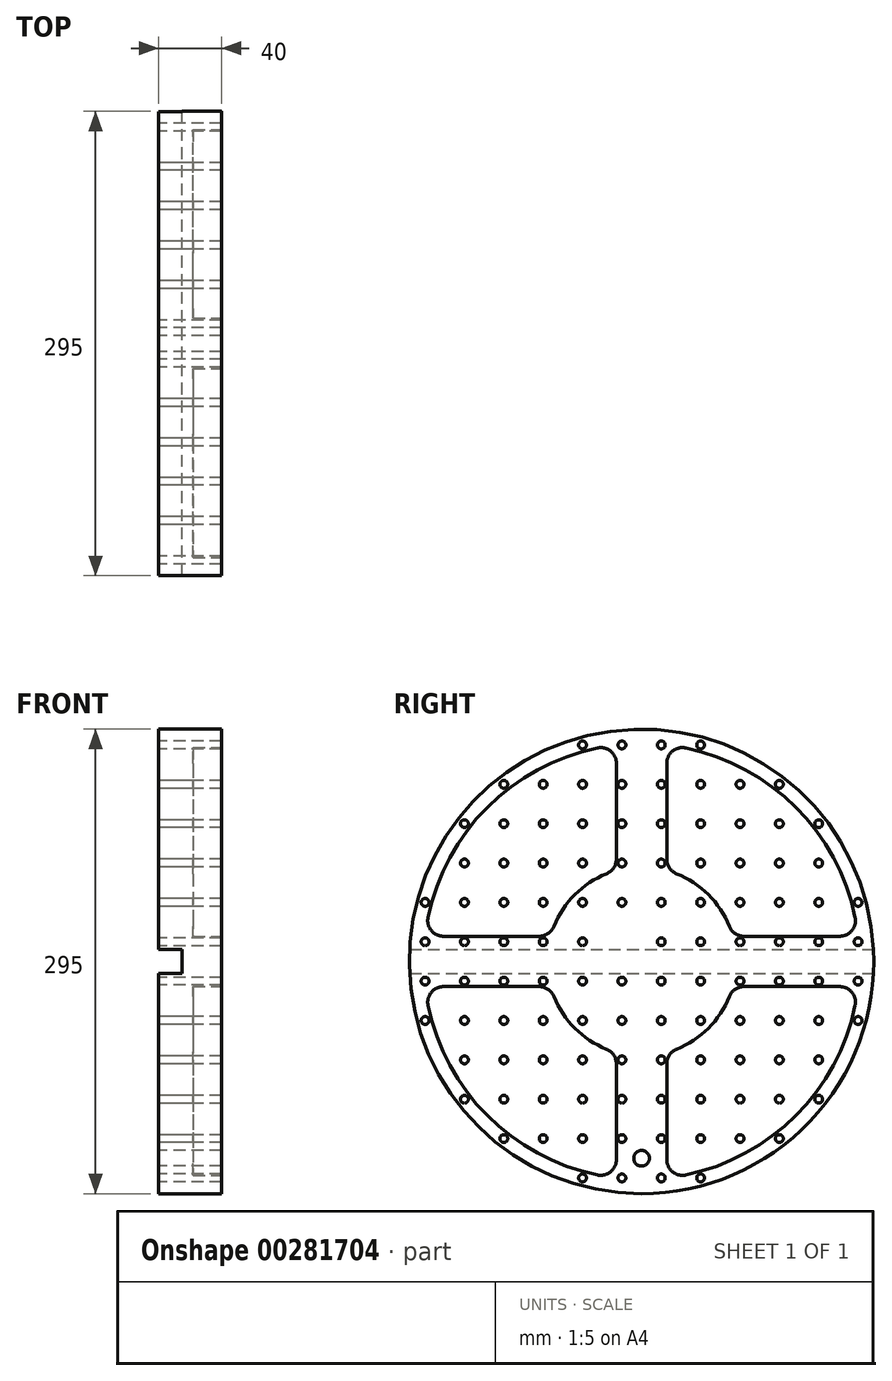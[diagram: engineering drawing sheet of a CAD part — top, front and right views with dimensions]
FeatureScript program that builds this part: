
annotation { "Feature Type Name" : "Feature", "Feature Type Description" : "" }
export const myFeature = defineFeature(function(context is Context, id is Id, definition is map)
    precondition{}
    {
        {
            var Q0;
            Q0=qCreatedBy(makeId("Right.planeOp"),FACE);
            var sketch = newSketch(context, id + "F0", { "sketchPlane" : qUnion([Q0])});
            skCircle(sketch, "E0", {"center": v(0, 0) * mm, "radius": 147.5 * mm});
            skLineSegment(sketch, "E1", {"start": v(-147.5, 0) * mm, "end": v(106.1, 0) * mm, "construction": true});
            skLineSegment(sketch, "E2", {"start": v(106.1, 0) * mm, "end": v(147.5, 0) * mm, "construction": true});
            skLineSegment(sketch, "E3", {"start": v(-147.3, 7.5) * mm, "end": v(147.3, 7.5) * mm});
            skLineSegment(sketch, "E4", {"start": v(-147.3, -7.5) * mm, "end": v(147.3, -7.5) * mm});
            skPoint(sketch, "E5.orphan", {"position": v(-155.54, -7.5) * mm});
            skCircle(sketch, "E6", {"center": v(-12.5, -12.5) * mm, "radius": 2.5 * mm});
            skCircle(sketch, "E7.0.1.0", {"center": v(-12.5, -37.5) * mm, "radius": 2.5 * mm});
            skCircle(sketch, "E7.0.2.0", {"center": v(-12.5, -62.5) * mm, "radius": 2.5 * mm});
            skCircle(sketch, "E7.0.3.0", {"center": v(-12.5, -87.5) * mm, "radius": 2.5 * mm});
            skCircle(sketch, "E7.1.0.0", {"center": v(-37.5, -12.5) * mm, "radius": 2.5 * mm});
            skCircle(sketch, "E7.1.1.0", {"center": v(-37.5, -37.5) * mm, "radius": 2.5 * mm});
            skCircle(sketch, "E7.1.2.0", {"center": v(-37.5, -62.5) * mm, "radius": 2.5 * mm});
            skCircle(sketch, "E7.1.3.0", {"center": v(-37.5, -87.5) * mm, "radius": 2.5 * mm});
            skCircle(sketch, "E7.2.0.0", {"center": v(-62.5, -12.5) * mm, "radius": 2.5 * mm});
            skCircle(sketch, "E7.2.1.0", {"center": v(-62.5, -37.5) * mm, "radius": 2.5 * mm});
            skCircle(sketch, "E7.2.2.0", {"center": v(-62.5, -62.5) * mm, "radius": 2.5 * mm});
            skCircle(sketch, "E7.2.3.0", {"center": v(-62.5, -87.5) * mm, "radius": 2.5 * mm});
            skCircle(sketch, "E7.3.0.0", {"center": v(-87.5, -12.5) * mm, "radius": 2.5 * mm});
            skCircle(sketch, "E7.3.1.0", {"center": v(-87.5, -37.5) * mm, "radius": 2.5 * mm});
            skCircle(sketch, "E7.3.2.0", {"center": v(-87.5, -62.5) * mm, "radius": 2.5 * mm});
            skCircle(sketch, "E7.3.3.0", {"center": v(-87.5, -87.5) * mm, "radius": 2.5 * mm});
            skLineSegment(sketch, "E7.direction1", {"start": v(-12.5, -12.5) * mm, "end": v(-37.5, -12.5) * mm, "construction": true});
            skLineSegment(sketch, "E7.direction2", {"start": v(-12.5, -12.5) * mm, "end": v(-12.5, -37.5) * mm, "construction": true});
            skCircle(sketch, "E8.0.0.4", {"center": v(-12.5, -112.5) * mm, "radius": 2.5 * mm});
            skCircle(sketch, "E8.0.1.4", {"center": v(-37.5, -112.5) * mm, "radius": 2.5 * mm});
            skCircle(sketch, "E8.0.2.4", {"center": v(-62.5, -112.5) * mm, "radius": 2.5 * mm});
            skCircle(sketch, "E8.0.3.4", {"center": v(-87.5, -112.5) * mm, "radius": 2.5 * mm});
            skCircle(sketch, "E9.0.0.5", {"center": v(-12.5, -137.5) * mm, "radius": 2.5 * mm});
            skCircle(sketch, "E9.0.1.5", {"center": v(-37.5, -137.5) * mm, "radius": 2.5 * mm});
            skCircle(sketch, "E9.0.2.5", {"center": v(-62.5, -137.5) * mm, "radius": 2.5 * mm});
            skCircle(sketch, "E9.0.3.5", {"center": v(-87.5, -137.5) * mm, "radius": 2.5 * mm});
            skCircle(sketch, "E10.0.4.0", {"center": v(-112.5, -12.5) * mm, "radius": 2.5 * mm});
            skCircle(sketch, "E10.0.4.1", {"center": v(-112.5, -37.5) * mm, "radius": 2.5 * mm});
            skCircle(sketch, "E10.0.4.2", {"center": v(-112.5, -62.5) * mm, "radius": 2.5 * mm});
            skCircle(sketch, "E10.0.4.3", {"center": v(-112.5, -87.5) * mm, "radius": 2.5 * mm});
            skCircle(sketch, "E10.0.4.4", {"center": v(-112.5, -112.5) * mm, "radius": 2.5 * mm});
            skCircle(sketch, "E10.0.4.5", {"center": v(-112.5, -137.5) * mm, "radius": 2.5 * mm});
            skCircle(sketch, "E10.0.5.0", {"center": v(-137.5, -12.5) * mm, "radius": 2.5 * mm});
            skCircle(sketch, "E10.0.5.1", {"center": v(-137.5, -37.5) * mm, "radius": 2.5 * mm});
            skCircle(sketch, "E10.0.5.2", {"center": v(-137.5, -62.5) * mm, "radius": 2.5 * mm});
            skCircle(sketch, "E10.0.5.3", {"center": v(-137.5, -87.5) * mm, "radius": 2.5 * mm});
            skCircle(sketch, "E10.0.5.4", {"center": v(-137.5, -112.5) * mm, "radius": 2.5 * mm});
            skCircle(sketch, "E10.0.5.5", {"center": v(-137.5, -137.5) * mm, "radius": 2.5 * mm});
            skCircle(sketch, "E11.MirrorC", {"center": v(87.5, -112.5) * mm, "radius": 2.5 * mm});
            skCircle(sketch, "E12.MirrorC", {"center": v(12.5, -112.5) * mm, "radius": 2.5 * mm});
            skCircle(sketch, "E13.MirrorC", {"center": v(62.5, -112.5) * mm, "radius": 2.5 * mm});
            skCircle(sketch, "E14.MirrorC", {"center": v(12.5, -12.5) * mm, "radius": 2.5 * mm});
            skCircle(sketch, "E15.MirrorC", {"center": v(37.5, -112.5) * mm, "radius": 2.5 * mm});
            skCircle(sketch, "E16.MirrorC", {"center": v(37.5, -12.5) * mm, "radius": 2.5 * mm});
            skCircle(sketch, "E17.MirrorC", {"center": v(12.5, -37.5) * mm, "radius": 2.5 * mm});
            skCircle(sketch, "E18.MirrorC", {"center": v(37.5, -87.5) * mm, "radius": 2.5 * mm});
            skCircle(sketch, "E19.MirrorC", {"center": v(12.5, -87.5) * mm, "radius": 2.5 * mm});
            skCircle(sketch, "E20.MirrorC", {"center": v(37.5, -137.5) * mm, "radius": 2.5 * mm});
            skCircle(sketch, "E21.MirrorC", {"center": v(62.5, -87.5) * mm, "radius": 2.5 * mm});
            skCircle(sketch, "E22.MirrorC", {"center": v(12.5, -62.5) * mm, "radius": 2.5 * mm});
            skCircle(sketch, "E23.MirrorC", {"center": v(87.5, -37.5) * mm, "radius": 2.5 * mm});
            skCircle(sketch, "E24.MirrorC", {"center": v(112.5, -37.5) * mm, "radius": 2.5 * mm});
            skCircle(sketch, "E25.MirrorC", {"center": v(112.5, -112.5) * mm, "radius": 2.5 * mm});
            skCircle(sketch, "E26.MirrorC", {"center": v(137.5, -62.5) * mm, "radius": 2.5 * mm});
            skCircle(sketch, "E27.MirrorC", {"center": v(87.5, -87.5) * mm, "radius": 2.5 * mm});
            skCircle(sketch, "E28.MirrorC", {"center": v(87.5, -12.5) * mm, "radius": 2.5 * mm});
            skCircle(sketch, "E29.MirrorC", {"center": v(137.5, -12.5) * mm, "radius": 2.5 * mm});
            skCircle(sketch, "E30.MirrorC", {"center": v(137.5, -137.5) * mm, "radius": 2.5 * mm});
            skCircle(sketch, "E31.MirrorC", {"center": v(112.5, -137.5) * mm, "radius": 2.5 * mm});
            skCircle(sketch, "E32.MirrorC", {"center": v(87.5, -137.5) * mm, "radius": 2.5 * mm});
            skCircle(sketch, "E33.MirrorC", {"center": v(137.5, -87.5) * mm, "radius": 2.5 * mm});
            skCircle(sketch, "E34.MirrorC", {"center": v(62.5, -62.5) * mm, "radius": 2.5 * mm});
            skCircle(sketch, "E35.MirrorC", {"center": v(12.5, -137.5) * mm, "radius": 2.5 * mm});
            skCircle(sketch, "E36.MirrorC", {"center": v(137.5, -112.5) * mm, "radius": 2.5 * mm});
            skCircle(sketch, "E37.MirrorC", {"center": v(112.5, -87.5) * mm, "radius": 2.5 * mm});
            skCircle(sketch, "E38.MirrorC", {"center": v(112.5, -62.5) * mm, "radius": 2.5 * mm});
            skCircle(sketch, "E39.MirrorC", {"center": v(37.5, -62.5) * mm, "radius": 2.5 * mm});
            skCircle(sketch, "E40.MirrorC", {"center": v(62.5, -137.5) * mm, "radius": 2.5 * mm});
            skCircle(sketch, "E41.MirrorC", {"center": v(62.5, -37.5) * mm, "radius": 2.5 * mm});
            skCircle(sketch, "E42.MirrorC", {"center": v(137.5, -37.5) * mm, "radius": 2.5 * mm});
            skCircle(sketch, "E43.MirrorC", {"center": v(112.5, -12.5) * mm, "radius": 2.5 * mm});
            skCircle(sketch, "E44.MirrorC", {"center": v(87.5, -62.5) * mm, "radius": 2.5 * mm});
            skCircle(sketch, "E45.MirrorC", {"center": v(62.5, -12.5) * mm, "radius": 2.5 * mm});
            skCircle(sketch, "E46.MirrorC", {"center": v(37.5, -37.5) * mm, "radius": 2.5 * mm});
            skLineSegment(sketch, "E47.MirrorCS", {"start": v(12.5, -12.5) * mm, "end": v(12.5, -37.5) * mm, "construction": true});
            skLineSegment(sketch, "E48.MirrorCS", {"start": v(12.5, -12.5) * mm, "end": v(37.5, -12.5) * mm, "construction": true});
            skLineSegment(sketch, "E49.MirrorCS", {"start": v(147.5, 0) * mm, "end": v(-106.1, 0) * mm, "construction": true});
            skCircle(sketch, "E50.MirrorC", {"center": v(-87.5, 112.5) * mm, "radius": 2.5 * mm});
            skCircle(sketch, "E51.MirrorC", {"center": v(-12.5, 12.5) * mm, "radius": 2.5 * mm});
            skCircle(sketch, "E52.MirrorC", {"center": v(87.5, 112.5) * mm, "radius": 2.5 * mm});
            skCircle(sketch, "E53.MirrorC", {"center": v(62.5, 112.5) * mm, "radius": 2.5 * mm});
            skCircle(sketch, "E54.MirrorC", {"center": v(12.5, 112.5) * mm, "radius": 2.5 * mm});
            skCircle(sketch, "E55.MirrorC", {"center": v(12.5, 12.5) * mm, "radius": 2.5 * mm});
            skCircle(sketch, "E56.MirrorC", {"center": v(-62.5, 112.5) * mm, "radius": 2.5 * mm});
            skCircle(sketch, "E57.MirrorC", {"center": v(37.5, 112.5) * mm, "radius": 2.5 * mm});
            skCircle(sketch, "E58.MirrorC", {"center": v(-37.5, 112.5) * mm, "radius": 2.5 * mm});
            skCircle(sketch, "E59.MirrorC", {"center": v(-12.5, 112.5) * mm, "radius": 2.5 * mm});
            skCircle(sketch, "E60.MirrorC", {"center": v(-12.5, 37.5) * mm, "radius": 2.5 * mm});
            skCircle(sketch, "E61.MirrorC", {"center": v(-37.5, 12.5) * mm, "radius": 2.5 * mm});
            skCircle(sketch, "E62.MirrorC", {"center": v(37.5, 12.5) * mm, "radius": 2.5 * mm});
            skCircle(sketch, "E63.MirrorC", {"center": v(12.5, 37.5) * mm, "radius": 2.5 * mm});
            skCircle(sketch, "E64.MirrorC", {"center": v(-62.5, 137.5) * mm, "radius": 2.5 * mm});
            skCircle(sketch, "E65.MirrorC", {"center": v(37.5, 87.5) * mm, "radius": 2.5 * mm});
            skCircle(sketch, "E66.MirrorC", {"center": v(-62.5, 37.5) * mm, "radius": 2.5 * mm});
            skCircle(sketch, "E67.MirrorC", {"center": v(37.5, 137.5) * mm, "radius": 2.5 * mm});
            skCircle(sketch, "E68.MirrorC", {"center": v(112.5, 12.5) * mm, "radius": 2.5 * mm});
            skCircle(sketch, "E69.MirrorC", {"center": v(62.5, 37.5) * mm, "radius": 2.5 * mm});
            skCircle(sketch, "E70.MirrorC", {"center": v(137.5, 37.5) * mm, "radius": 2.5 * mm});
            skCircle(sketch, "E71.MirrorC", {"center": v(37.5, 37.5) * mm, "radius": 2.5 * mm});
            skCircle(sketch, "E72.MirrorC", {"center": v(12.5, 137.5) * mm, "radius": 2.5 * mm});
            skCircle(sketch, "E73.MirrorC", {"center": v(137.5, 137.5) * mm, "radius": 2.5 * mm});
            skCircle(sketch, "E74.MirrorC", {"center": v(62.5, 87.5) * mm, "radius": 2.5 * mm});
            skCircle(sketch, "E75.MirrorC", {"center": v(-62.5, 87.5) * mm, "radius": 2.5 * mm});
            skCircle(sketch, "E76.MirrorC", {"center": v(-87.5, 87.5) * mm, "radius": 2.5 * mm});
            skCircle(sketch, "E77.MirrorC", {"center": v(37.5, 62.5) * mm, "radius": 2.5 * mm});
            skCircle(sketch, "E78.MirrorC", {"center": v(112.5, 37.5) * mm, "radius": 2.5 * mm});
            skCircle(sketch, "E79.MirrorC", {"center": v(-112.5, 87.5) * mm, "radius": 2.5 * mm});
            skCircle(sketch, "E80.MirrorC", {"center": v(112.5, 112.5) * mm, "radius": 2.5 * mm});
            skCircle(sketch, "E81.MirrorC", {"center": v(-112.5, 12.5) * mm, "radius": 2.5 * mm});
            skCircle(sketch, "E82.MirrorC", {"center": v(-112.5, 37.5) * mm, "radius": 2.5 * mm});
            skCircle(sketch, "E83.MirrorC", {"center": v(-37.5, 37.5) * mm, "radius": 2.5 * mm});
            skCircle(sketch, "E84.MirrorC", {"center": v(62.5, 137.5) * mm, "radius": 2.5 * mm});
            skCircle(sketch, "E85.MirrorC", {"center": v(-87.5, 137.5) * mm, "radius": 2.5 * mm});
            skCircle(sketch, "E86.MirrorC", {"center": v(112.5, 62.5) * mm, "radius": 2.5 * mm});
            skCircle(sketch, "E87.MirrorC", {"center": v(-37.5, 137.5) * mm, "radius": 2.5 * mm});
            skCircle(sketch, "E88.MirrorC", {"center": v(87.5, 62.5) * mm, "radius": 2.5 * mm});
            skCircle(sketch, "E89.MirrorC", {"center": v(-62.5, 12.5) * mm, "radius": 2.5 * mm});
            skCircle(sketch, "E90.MirrorC", {"center": v(137.5, 87.5) * mm, "radius": 2.5 * mm});
            skCircle(sketch, "E91.MirrorC", {"center": v(-12.5, 137.5) * mm, "radius": 2.5 * mm});
            skCircle(sketch, "E92.MirrorC", {"center": v(-137.5, 87.5) * mm, "radius": 2.5 * mm});
            skCircle(sketch, "E93.MirrorC", {"center": v(137.5, 12.5) * mm, "radius": 2.5 * mm});
            skCircle(sketch, "E94.MirrorC", {"center": v(-137.5, 12.5) * mm, "radius": 2.5 * mm});
            skCircle(sketch, "E95.MirrorC", {"center": v(87.5, 87.5) * mm, "radius": 2.5 * mm});
            skCircle(sketch, "E96.MirrorC", {"center": v(12.5, 62.5) * mm, "radius": 2.5 * mm});
            skCircle(sketch, "E97.MirrorC", {"center": v(-12.5, 62.5) * mm, "radius": 2.5 * mm});
            skCircle(sketch, "E98.MirrorC", {"center": v(-137.5, 62.5) * mm, "radius": 2.5 * mm});
            skCircle(sketch, "E99.MirrorC", {"center": v(62.5, 12.5) * mm, "radius": 2.5 * mm});
            skCircle(sketch, "E100.MirrorC", {"center": v(-62.5, 62.5) * mm, "radius": 2.5 * mm});
            skCircle(sketch, "E101.MirrorC", {"center": v(87.5, 12.5) * mm, "radius": 2.5 * mm});
            skCircle(sketch, "E102.MirrorC", {"center": v(-37.5, 87.5) * mm, "radius": 2.5 * mm});
            skCircle(sketch, "E103.MirrorC", {"center": v(-87.5, 37.5) * mm, "radius": 2.5 * mm});
            skCircle(sketch, "E104.MirrorC", {"center": v(12.5, 87.5) * mm, "radius": 2.5 * mm});
            skCircle(sketch, "E105.MirrorC", {"center": v(112.5, 87.5) * mm, "radius": 2.5 * mm});
            skCircle(sketch, "E106.MirrorC", {"center": v(-112.5, 62.5) * mm, "radius": 2.5 * mm});
            skCircle(sketch, "E107.MirrorC", {"center": v(-87.5, 62.5) * mm, "radius": 2.5 * mm});
            skCircle(sketch, "E108.MirrorC", {"center": v(-137.5, 137.5) * mm, "radius": 2.5 * mm});
            skCircle(sketch, "E109.MirrorC", {"center": v(-112.5, 112.5) * mm, "radius": 2.5 * mm});
            skCircle(sketch, "E110.MirrorC", {"center": v(-112.5, 137.5) * mm, "radius": 2.5 * mm});
            skCircle(sketch, "E111.MirrorC", {"center": v(137.5, 62.5) * mm, "radius": 2.5 * mm});
            skCircle(sketch, "E112.MirrorC", {"center": v(-12.5, 87.5) * mm, "radius": 2.5 * mm});
            skCircle(sketch, "E113.MirrorC", {"center": v(-87.5, 12.5) * mm, "radius": 2.5 * mm});
            skCircle(sketch, "E114.MirrorC", {"center": v(-137.5, 112.5) * mm, "radius": 2.5 * mm});
            skCircle(sketch, "E115.MirrorC", {"center": v(137.5, 112.5) * mm, "radius": 2.5 * mm});
            skCircle(sketch, "E116.MirrorC", {"center": v(62.5, 62.5) * mm, "radius": 2.5 * mm});
            skCircle(sketch, "E117.MirrorC", {"center": v(87.5, 37.5) * mm, "radius": 2.5 * mm});
            skCircle(sketch, "E118.MirrorC", {"center": v(-137.5, 37.5) * mm, "radius": 2.5 * mm});
            skCircle(sketch, "E119.MirrorC", {"center": v(-37.5, 62.5) * mm, "radius": 2.5 * mm});
            skCircle(sketch, "E120.MirrorC", {"center": v(112.5, 137.5) * mm, "radius": 2.5 * mm});
            skCircle(sketch, "E121.MirrorC", {"center": v(87.5, 137.5) * mm, "radius": 2.5 * mm});
            skLineSegment(sketch, "E122.MirrorCS", {"start": v(12.5, 12.5) * mm, "end": v(12.5, 37.5) * mm, "construction": true});
            skLineSegment(sketch, "E123.MirrorCS", {"start": v(12.5, 12.5) * mm, "end": v(37.5, 12.5) * mm, "construction": true});
            skLineSegment(sketch, "E124.MirrorCS", {"start": v(-12.5, 12.5) * mm, "end": v(-37.5, 12.5) * mm, "construction": true});
            skLineSegment(sketch, "E125.MirrorCS", {"start": v(-12.5, 12.5) * mm, "end": v(-12.5, 37.5) * mm, "construction": true});
            skPoint(sketch, "E126.MirrorP", {"position": v(-155.54, 7.5) * mm});
            skLineSegment(sketch, "E127", {"start": v(12.5, -112.5) * mm, "end": v(-12.5, -137.5) * mm, "construction": true});
            skLineSegment(sketch, "E128", {"start": v(-12.5, -112.5) * mm, "end": v(12.5, -137.5) * mm, "construction": true});
            skPoint(sketch, "E129", {"position": v(0, -125) * mm});
            skCircle(sketch, "E130", {"center": v(0, -125) * mm, "radius": 5 * mm});
            skSolve(sketch);
        }
        {
            var Q0;
            Q0=makeQuery(id+"F0.imprint","IMPRINT",FACE,{"disambiguationData":[TD([[makeQuery(id+"F0.imprint","IMPRINT",EDGE,{"derivedFrom":sQuery(id+"F0.wireOp",EDGE,"IFr8vejr-TE2V-nbfY-BL64-3zSkw80Edfo5")}),-1.0]])]});
            var Q1;
            Q1=makeQuery(id+"F0.imprint","IMPRINT",FACE,{"disambiguationData":[TD([[makeQuery(id+"F0.imprint","IMPRINT",EDGE,{"derivedFrom":sQuery(id+"F0.wireOp",EDGE,"f1ff1820-f697-4541-9928-8c9d74d6425a.6.0")}),-1.0]])]});
            var Q2;
            Q2=makeQuery(id+"F0.imprint","IMPRINT",FACE,{"disambiguationData":[TD([[makeQuery(id+"F0.imprint","IMPRINT",EDGE,{"derivedFrom":sQuery(id+"F0.wireOp",EDGE,"GyFtQHSs-FAC8-PiSM-a0nY-W9q30hJzTPO9")}),-1.0]])]});
            var Q3;
            {var subQ0=sQuery(id+"F0.wireOp",EDGE,"E4");Q3=makeQuery(id+"F0.imprint","IMPRINT",FACE,{"disambiguationData":[TD([[makeQuery(id+"F0.imprint","IMPRINT",EDGE,{"derivedFrom":subQ0}),-1.0]])]});}
            var Q4;
            {var subQ0=sQuery(id+"F0.wireOp",EDGE,"E3");Q4=makeQuery(id+"F0.imprint","IMPRINT",FACE,{"disambiguationData":[TD([[makeQuery(id+"F0.imprint","IMPRINT",EDGE,{"derivedFrom":subQ0}),1.0]])]});}
            var Q5;
            {var subQ0=sQuery(id+"F0.wireOp",EDGE,"E3");Q5=makeQuery(id+"F0.imprint","IMPRINT",FACE,{"disambiguationData":[TD([[makeQuery(id+"F0.imprint","IMPRINT",EDGE,{"derivedFrom":subQ0}),-1.0]])]});}
            var Q6;
            Q6=makeQuery(id+"F0.imprint","IMPRINT",FACE,{"disambiguationData":[TD([[makeQuery(id+"F0.imprint","IMPRINT",EDGE,{"derivedFrom":sQuery(id+"F0.wireOp",EDGE,"E51.MirrorC")}),1.0]])]});
            var Q7;
            {var subQ0=sQuery(id+"F0.wireOp",EDGE,"E4");Q7=makeQuery(id+"F0.imprint","IMPRINT",FACE,{"disambiguationData":[TD([[makeQuery(id+"F0.imprint","IMPRINT",EDGE,{"derivedFrom":subQ0}),1.0]])]});}
            extrude(context, id + "F1", {"entities" : qUnion([Q0, Q1, Q2, Q3, Q4, Q5, Q6, Q7]), "depth" : 40 * mm, "offsetDistance" : 25 * mm});
        }
        {
            var Q0;
            Q0=makeQuery(id+"F1.opExtrude","CAP_FACE",FACE,{"disambiguationData":[OSD([sQuery(id+"F0.wireOp",EDGE,"E0"),sQuery(id+"F0.wireOp",EDGE,"IFr8vejr-TE2V-nbfY-BL64-3zSkw80Edfo5"),sQuery(id+"F0.wireOp",EDGE,"ni2gV7jt-xXpM-BkHP-OWPN-ODkOcCd5O03l"),sQuery(id+"F0.wireOp",EDGE,"GyFtQHSs-FAC8-PiSM-a0nY-W9q30hJzTPO9"),sQuery(id+"F0.wireOp",EDGE,"3THfQWAF-OsD5-m8qg-8VvL-ybaqfSjL85Ep"),sQuery(id+"F0.wireOp",EDGE,"124ff6b1-3ffd-4921-9cf3-9a8699d24955.0.1.0"),sQuery(id+"F0.wireOp",EDGE,"124ff6b1-3ffd-4921-9cf3-9a8699d24955.0.2.0"),sQuery(id+"F0.wireOp",EDGE,"124ff6b1-3ffd-4921-9cf3-9a8699d24955.0.3.0"),sQuery(id+"F0.wireOp",EDGE,"124ff6b1-3ffd-4921-9cf3-9a8699d24955.1.0.0"),sQuery(id+"F0.wireOp",EDGE,"124ff6b1-3ffd-4921-9cf3-9a8699d24955.1.1.0"),sQuery(id+"F0.wireOp",EDGE,"124ff6b1-3ffd-4921-9cf3-9a8699d24955.1.2.0"),sQuery(id+"F0.wireOp",EDGE,"124ff6b1-3ffd-4921-9cf3-9a8699d24955.1.3.0"),sQuery(id+"F0.wireOp",EDGE,"124ff6b1-3ffd-4921-9cf3-9a8699d24955.2.0.0"),sQuery(id+"F0.wireOp",EDGE,"124ff6b1-3ffd-4921-9cf3-9a8699d24955.2.1.0"),sQuery(id+"F0.wireOp",EDGE,"124ff6b1-3ffd-4921-9cf3-9a8699d24955.2.2.0"),sQuery(id+"F0.wireOp",EDGE,"124ff6b1-3ffd-4921-9cf3-9a8699d24955.2.3.0"),sQuery(id+"F0.wireOp",EDGE,"124ff6b1-3ffd-4921-9cf3-9a8699d24955.3.0.0"),sQuery(id+"F0.wireOp",EDGE,"124ff6b1-3ffd-4921-9cf3-9a8699d24955.3.1.0"),sQuery(id+"F0.wireOp",EDGE,"124ff6b1-3ffd-4921-9cf3-9a8699d24955.3.2.0"),sQuery(id+"F0.wireOp",EDGE,"124ff6b1-3ffd-4921-9cf3-9a8699d24955.3.3.0"),sQuery(id+"F0.wireOp",EDGE,"2f6fac57-cf5a-4152-9429-d766ee51de16.0.1.0"),sQuery(id+"F0.wireOp",EDGE,"2f6fac57-cf5a-4152-9429-d766ee51de16.0.2.0"),sQuery(id+"F0.wireOp",EDGE,"2f6fac57-cf5a-4152-9429-d766ee51de16.0.3.0"),sQuery(id+"F0.wireOp",EDGE,"2f6fac57-cf5a-4152-9429-d766ee51de16.1.0.0"),sQuery(id+"F0.wireOp",EDGE,"2f6fac57-cf5a-4152-9429-d766ee51de16.1.1.0"),sQuery(id+"F0.wireOp",EDGE,"2f6fac57-cf5a-4152-9429-d766ee51de16.1.2.0"),sQuery(id+"F0.wireOp",EDGE,"2f6fac57-cf5a-4152-9429-d766ee51de16.1.3.0"),sQuery(id+"F0.wireOp",EDGE,"2f6fac57-cf5a-4152-9429-d766ee51de16.2.0.0"),sQuery(id+"F0.wireOp",EDGE,"2f6fac57-cf5a-4152-9429-d766ee51de16.2.1.0"),sQuery(id+"F0.wireOp",EDGE,"2f6fac57-cf5a-4152-9429-d766ee51de16.2.2.0"),sQuery(id+"F0.wireOp",EDGE,"2f6fac57-cf5a-4152-9429-d766ee51de16.2.3.0"),sQuery(id+"F0.wireOp",EDGE,"2f6fac57-cf5a-4152-9429-d766ee51de16.3.0.0"),sQuery(id+"F0.wireOp",EDGE,"2f6fac57-cf5a-4152-9429-d766ee51de16.3.1.0"),sQuery(id+"F0.wireOp",EDGE,"2f6fac57-cf5a-4152-9429-d766ee51de16.3.2.0"),sQuery(id+"F0.wireOp",EDGE,"2f6fac57-cf5a-4152-9429-d766ee51de16.3.3.0"),sQuery(id+"F0.wireOp",EDGE,"32b1d0c1-1f6d-4e5e-8add-1ff7e260cb1f.0.1.0"),sQuery(id+"F0.wireOp",EDGE,"32b1d0c1-1f6d-4e5e-8add-1ff7e260cb1f.0.2.0"),sQuery(id+"F0.wireOp",EDGE,"32b1d0c1-1f6d-4e5e-8add-1ff7e260cb1f.0.3.0"),sQuery(id+"F0.wireOp",EDGE,"32b1d0c1-1f6d-4e5e-8add-1ff7e260cb1f.1.0.0"),sQuery(id+"F0.wireOp",EDGE,"32b1d0c1-1f6d-4e5e-8add-1ff7e260cb1f.1.1.0"),sQuery(id+"F0.wireOp",EDGE,"32b1d0c1-1f6d-4e5e-8add-1ff7e260cb1f.1.2.0"),sQuery(id+"F0.wireOp",EDGE,"32b1d0c1-1f6d-4e5e-8add-1ff7e260cb1f.1.3.0"),sQuery(id+"F0.wireOp",EDGE,"32b1d0c1-1f6d-4e5e-8add-1ff7e260cb1f.2.0.0"),sQuery(id+"F0.wireOp",EDGE,"32b1d0c1-1f6d-4e5e-8add-1ff7e260cb1f.2.1.0"),sQuery(id+"F0.wireOp",EDGE,"32b1d0c1-1f6d-4e5e-8add-1ff7e260cb1f.2.2.0"),sQuery(id+"F0.wireOp",EDGE,"32b1d0c1-1f6d-4e5e-8add-1ff7e260cb1f.2.3.0"),sQuery(id+"F0.wireOp",EDGE,"32b1d0c1-1f6d-4e5e-8add-1ff7e260cb1f.3.0.0"),sQuery(id+"F0.wireOp",EDGE,"32b1d0c1-1f6d-4e5e-8add-1ff7e260cb1f.3.1.0"),sQuery(id+"F0.wireOp",EDGE,"32b1d0c1-1f6d-4e5e-8add-1ff7e260cb1f.3.2.0"),sQuery(id+"F0.wireOp",EDGE,"32b1d0c1-1f6d-4e5e-8add-1ff7e260cb1f.3.3.0"),sQuery(id+"F0.wireOp",EDGE,"dfcd6cd3-9c83-4150-b3b6-5a39950986eb.0.1.0"),sQuery(id+"F0.wireOp",EDGE,"dfcd6cd3-9c83-4150-b3b6-5a39950986eb.0.2.0"),sQuery(id+"F0.wireOp",EDGE,"dfcd6cd3-9c83-4150-b3b6-5a39950986eb.0.3.0"),sQuery(id+"F0.wireOp",EDGE,"dfcd6cd3-9c83-4150-b3b6-5a39950986eb.1.0.0"),sQuery(id+"F0.wireOp",EDGE,"dfcd6cd3-9c83-4150-b3b6-5a39950986eb.1.1.0"),sQuery(id+"F0.wireOp",EDGE,"dfcd6cd3-9c83-4150-b3b6-5a39950986eb.1.2.0"),sQuery(id+"F0.wireOp",EDGE,"dfcd6cd3-9c83-4150-b3b6-5a39950986eb.1.3.0"),sQuery(id+"F0.wireOp",EDGE,"dfcd6cd3-9c83-4150-b3b6-5a39950986eb.2.0.0"),sQuery(id+"F0.wireOp",EDGE,"dfcd6cd3-9c83-4150-b3b6-5a39950986eb.2.1.0"),sQuery(id+"F0.wireOp",EDGE,"dfcd6cd3-9c83-4150-b3b6-5a39950986eb.2.2.0"),sQuery(id+"F0.wireOp",EDGE,"dfcd6cd3-9c83-4150-b3b6-5a39950986eb.2.3.0"),sQuery(id+"F0.wireOp",EDGE,"dfcd6cd3-9c83-4150-b3b6-5a39950986eb.3.0.0"),sQuery(id+"F0.wireOp",EDGE,"dfcd6cd3-9c83-4150-b3b6-5a39950986eb.3.1.0"),sQuery(id+"F0.wireOp",EDGE,"dfcd6cd3-9c83-4150-b3b6-5a39950986eb.3.2.0"),sQuery(id+"F0.wireOp",EDGE,"dfcd6cd3-9c83-4150-b3b6-5a39950986eb.3.3.0"),sQuery(id+"F0.wireOp",EDGE,"dYsYgjIR-hnB1-luYH-05GF-c5KB9xP18FLt"),sQuery(id+"F0.wireOp",EDGE,"716dc1ae-e0b3-4284-aa59-d3373ff65dcd.0.1.0"),sQuery(id+"F0.wireOp",EDGE,"716dc1ae-e0b3-4284-aa59-d3373ff65dcd.0.2.0"),sQuery(id+"F0.wireOp",EDGE,"716dc1ae-e0b3-4284-aa59-d3373ff65dcd.0.3.0"),sQuery(id+"F0.wireOp",EDGE,"haXRSSE7-RhOz-70Uj-Y6ZE-75GEVdKYXfgl"),sQuery(id+"F0.wireOp",EDGE,"5a910c27-c7f2-48b4-a220-f8e7ce144880.0.1.0"),sQuery(id+"F0.wireOp",EDGE,"5a910c27-c7f2-48b4-a220-f8e7ce144880.0.2.0"),sQuery(id+"F0.wireOp",EDGE,"5a910c27-c7f2-48b4-a220-f8e7ce144880.0.3.0"),sQuery(id+"F0.wireOp",EDGE,"c11f6003-ca0d-4695-bfd2-25a3abb8dbd0.0.1.0"),sQuery(id+"F0.wireOp",EDGE,"c11f6003-ca0d-4695-bfd2-25a3abb8dbd0.0.1.1"),sQuery(id+"F0.wireOp",EDGE,"c11f6003-ca0d-4695-bfd2-25a3abb8dbd0.0.1.2"),sQuery(id+"F0.wireOp",EDGE,"c11f6003-ca0d-4695-bfd2-25a3abb8dbd0.0.1.3"),sQuery(id+"F0.wireOp",EDGE,"b142fc62-8894-4678-a877-5f8a7ab5144e.0.1.0"),sQuery(id+"F0.wireOp",EDGE,"b142fc62-8894-4678-a877-5f8a7ab5144e.0.1.1"),sQuery(id+"F0.wireOp",EDGE,"b142fc62-8894-4678-a877-5f8a7ab5144e.0.1.2"),sQuery(id+"F0.wireOp",EDGE,"b142fc62-8894-4678-a877-5f8a7ab5144e.0.1.3"),sQuery(id+"F0.wireOp",EDGE,"0a2bd74c-fd9d-421f-9e4f-b3f75c92df6b"),sQuery(id+"F0.wireOp",EDGE,"f1ff1820-f697-4541-9928-8c9d74d6425a.1.0"),sQuery(id+"F0.wireOp",EDGE,"f1ff1820-f697-4541-9928-8c9d74d6425a.3.0"),sQuery(id+"F0.wireOp",EDGE,"f1ff1820-f697-4541-9928-8c9d74d6425a.4.0"),sQuery(id+"F0.wireOp",EDGE,"f1ff1820-f697-4541-9928-8c9d74d6425a.5.0"),sQuery(id+"F0.wireOp",EDGE,"f1ff1820-f697-4541-9928-8c9d74d6425a.6.0"),sQuery(id+"F0.wireOp",EDGE,"f1ff1820-f697-4541-9928-8c9d74d6425a.7.0"),sQuery(id+"F0.wireOp",EDGE,"f1e9a0f9-fb49-41d8-9eed-0eeb2a145c22.1.0"),sQuery(id+"F0.wireOp",EDGE,"bccd33c4-be98-4848-a069-18523a92b7b0.1.0"),sQuery(id+"F0.wireOp",EDGE,"bccd33c4-be98-4848-a069-18523a92b7b0.2.0"),sQuery(id+"F0.wireOp",EDGE,"bccd33c4-be98-4848-a069-18523a92b7b0.3.0"),sQuery(id+"F0.wireOp",EDGE,"bccd33c4-be98-4848-a069-18523a92b7b0.4.0"),sQuery(id+"F0.wireOp",EDGE,"bccd33c4-be98-4848-a069-18523a92b7b0.5.0"),sQuery(id+"F0.wireOp",EDGE,"bccd33c4-be98-4848-a069-18523a92b7b0.6.0"),sQuery(id+"F0.wireOp",EDGE,"bccd33c4-be98-4848-a069-18523a92b7b0.7.0")])],"isStart":false});
            var sketch = newSketch(context, id + "F2", { "sketchPlane" : qUnion([Q0])});
            skArc(sketch, "E131", {"start": v(-22.29, 55.7) * mm, "mid": v(-42.43, 42.43) * mm, "end": v(-55.7, 22.29) * mm});
            skArc(sketch, "E132", {"start": v(-135.64, -28.02) * mm, "mid": v(-97.93, -97.93) * mm, "end": v(-28.02, -135.64) * mm});
            skLineSegment(sketch, "E133", {"start": v(-125.84, 16) * mm, "end": v(-65, 16) * mm});
            skLineSegment(sketch, "E134", {"start": v(-125.84, -16) * mm, "end": v(-65, -16) * mm});
            skLineSegment(sketch, "E135", {"start": v(-16, 125.84) * mm, "end": v(-16, 65) * mm});
            skLineSegment(sketch, "E136", {"start": v(16, 125.84) * mm, "end": v(16, 65) * mm});
            skPoint(sketch, "E137.orphan", {"position": v(-16, -169.8) * mm});
            skPoint(sketch, "E138.orphan", {"position": v(16, -169.8) * mm});
            skLineSegment(sketch, "E139.trimOffspring", {"start": v(-16, -65) * mm, "end": v(-16, -125.84) * mm});
            skLineSegment(sketch, "E140.trimOffspring", {"start": v(65, 16) * mm, "end": v(125.84, 16) * mm});
            skLineSegment(sketch, "E141.trimOffspring", {"start": v(16, -65) * mm, "end": v(16, -125.84) * mm});
            skLineSegment(sketch, "E142.trimOffspring", {"start": v(65, -16) * mm, "end": v(125.84, -16) * mm});
            skArc(sketch, "E143.trimOffspring", {"start": v(-28.02, 135.64) * mm, "mid": v(-97.93, 97.93) * mm, "end": v(-135.64, 28.02) * mm});
            skArc(sketch, "E144.trimOffspring", {"start": v(135.64, 28.02) * mm, "mid": v(97.93, 97.93) * mm, "end": v(28.02, 135.64) * mm});
            skArc(sketch, "E145.trimOffspring", {"start": v(28.02, -135.64) * mm, "mid": v(97.93, -97.93) * mm, "end": v(135.64, -28.02) * mm});
            skPoint(sketch, "E146.visualSharp", {"position": v(-137.57, 16) * mm});
            skArc(sketch, "E146.filletArc", {"start": v(-135.71, 27.6) * mm, "mid": v(-133.46, 19.52) * mm, "end": v(-125.84, 16) * mm});
            skArc(sketch, "E147.filletArc", {"start": v(-135.64, 28.02) * mm, "mid": v(-133.6, 19.68) * mm, "end": v(-125.84, 16) * mm});
            skPoint(sketch, "E148.visualSharp", {"position": v(-16, 137.57) * mm});
            skArc(sketch, "E148.filletArc", {"start": v(-16, 125.84) * mm, "mid": v(-19.68, 133.6) * mm, "end": v(-28.02, 135.64) * mm});
            skPoint(sketch, "E149.visualSharp", {"position": v(16, 137.57) * mm});
            skArc(sketch, "E149.filletArc", {"start": v(28.02, 135.64) * mm, "mid": v(19.68, 133.6) * mm, "end": v(16, 125.84) * mm});
            skPoint(sketch, "E150.visualSharp", {"position": v(137.57, 16) * mm});
            skArc(sketch, "E150.filletArc", {"start": v(125.84, 16) * mm, "mid": v(133.6, 19.68) * mm, "end": v(135.64, 28.02) * mm});
            skPoint(sketch, "E151.visualSharp", {"position": v(137.57, -16) * mm});
            skArc(sketch, "E151.filletArc", {"start": v(135.64, -28.02) * mm, "mid": v(133.6, -19.68) * mm, "end": v(125.84, -16) * mm});
            skPoint(sketch, "E152.visualSharp", {"position": v(16, -137.57) * mm});
            skArc(sketch, "E152.filletArc", {"start": v(16, -125.84) * mm, "mid": v(19.68, -133.6) * mm, "end": v(28.02, -135.64) * mm});
            skPoint(sketch, "E153.visualSharp", {"position": v(-16, -137.57) * mm});
            skArc(sketch, "E153.filletArc", {"start": v(-28.02, -135.64) * mm, "mid": v(-19.68, -133.6) * mm, "end": v(-16, -125.84) * mm});
            skPoint(sketch, "E154.visualSharp", {"position": v(-137.57, -16) * mm});
            skArc(sketch, "E154.filletArc", {"start": v(-125.84, -16) * mm, "mid": v(-133.6, -19.68) * mm, "end": v(-135.64, -28.02) * mm});
            skArc(sketch, "E155.trimOffspring", {"start": v(-55.7, -22.29) * mm, "mid": v(-42.43, -42.43) * mm, "end": v(-22.29, -55.7) * mm});
            skArc(sketch, "E156.trimOffspring", {"start": v(22.29, -55.7) * mm, "mid": v(42.43, -42.43) * mm, "end": v(55.7, -22.29) * mm});
            skArc(sketch, "E157.trimOffspring", {"start": v(55.7, 22.29) * mm, "mid": v(42.43, 42.43) * mm, "end": v(22.29, 55.7) * mm});
            skPoint(sketch, "E158.visualSharp", {"position": v(-57.83, 16) * mm});
            skArc(sketch, "E158.filletArc", {"start": v(-65, 16) * mm, "mid": v(-59.39, 17.72) * mm, "end": v(-55.7, 22.29) * mm});
            skPoint(sketch, "E159.visualSharp", {"position": v(-16, 57.83) * mm});
            skArc(sketch, "E159.filletArc", {"start": v(-22.29, 55.7) * mm, "mid": v(-17.72, 59.39) * mm, "end": v(-16, 65) * mm});
            skPoint(sketch, "E160.visualSharp", {"position": v(16, 57.83) * mm});
            skArc(sketch, "E160.filletArc", {"start": v(16, 65) * mm, "mid": v(17.72, 59.39) * mm, "end": v(22.29, 55.7) * mm});
            skPoint(sketch, "E161.visualSharp", {"position": v(57.83, 16) * mm});
            skArc(sketch, "E161.filletArc", {"start": v(55.7, 22.29) * mm, "mid": v(59.39, 17.72) * mm, "end": v(65, 16) * mm});
            skPoint(sketch, "E162.visualSharp", {"position": v(57.83, -16) * mm});
            skArc(sketch, "E162.filletArc", {"start": v(65, -16) * mm, "mid": v(59.39, -17.72) * mm, "end": v(55.7, -22.29) * mm});
            skPoint(sketch, "E163.visualSharp", {"position": v(16, -57.83) * mm});
            skArc(sketch, "E163.filletArc", {"start": v(22.29, -55.7) * mm, "mid": v(17.72, -59.39) * mm, "end": v(16, -65) * mm});
            skPoint(sketch, "E164.visualSharp", {"position": v(-16, -57.83) * mm});
            skArc(sketch, "E164.filletArc", {"start": v(-16, -65) * mm, "mid": v(-17.72, -59.39) * mm, "end": v(-22.29, -55.7) * mm});
            skPoint(sketch, "E165.visualSharp", {"position": v(-57.83, -16) * mm});
            skArc(sketch, "E165.filletArc", {"start": v(-55.7, -22.29) * mm, "mid": v(-59.39, -17.72) * mm, "end": v(-65, -16) * mm});
            skSolve(sketch);
        }
        {
            var Q0;
            {var subQ0=sQuery(id+"F0.wireOp",EDGE,"E4");Q0=makeQuery(id+"F0.imprint","IMPRINT",FACE,{"disambiguationData":[TD([[makeQuery(id+"F0.imprint","IMPRINT",EDGE,{"derivedFrom":subQ0}),1.0]])]});}
            extrude(context, id + "F3", {"entities" : qUnion([Q0]), "operationType" : NewBodyOperationType.REMOVE, "depth" : 15 * mm, "offsetDistance" : 25 * mm});
        }
        {
            var Q0;
            Q0=makeQuery(id+"F2.imprint","IMPRINT",FACE,{"disambiguationData":[TD([[makeQuery(id+"F2.imprint","IMPRINT",EDGE,{"derivedFrom":sQuery(id+"F2.wireOp",EDGE,"E131")}),-1.0]])]});
            var Q1;
            Q1=makeQuery(id+"F2.imprint","IMPRINT",FACE,{"disambiguationData":[TD([[makeQuery(id+"F2.imprint","IMPRINT",EDGE,{"derivedFrom":sQuery(id+"F2.wireOp",EDGE,"E132")}),1.0]])]});
            var Q2;
            Q2=makeQuery(id+"F2.imprint","IMPRINT",FACE,{"disambiguationData":[TD([[makeQuery(id+"F2.imprint","IMPRINT",EDGE,{"derivedFrom":sQuery(id+"F2.wireOp",EDGE,"E141.trimOffspring")}),1.0]])]});
            var Q3;
            Q3=makeQuery(id+"F2.imprint","IMPRINT",FACE,{"disambiguationData":[TD([[makeQuery(id+"F2.imprint","IMPRINT",EDGE,{"derivedFrom":sQuery(id+"F2.wireOp",EDGE,"E136")}),1.0]])]});
            extrude(context, id + "F4", {"entities" : qUnion([Q0, Q1, Q2, Q3]), "operationType" : NewBodyOperationType.REMOVE, "oppositeDirection" : true, "depth" : 18 * mm, "offsetDistance" : 25 * mm});
        }
    });
